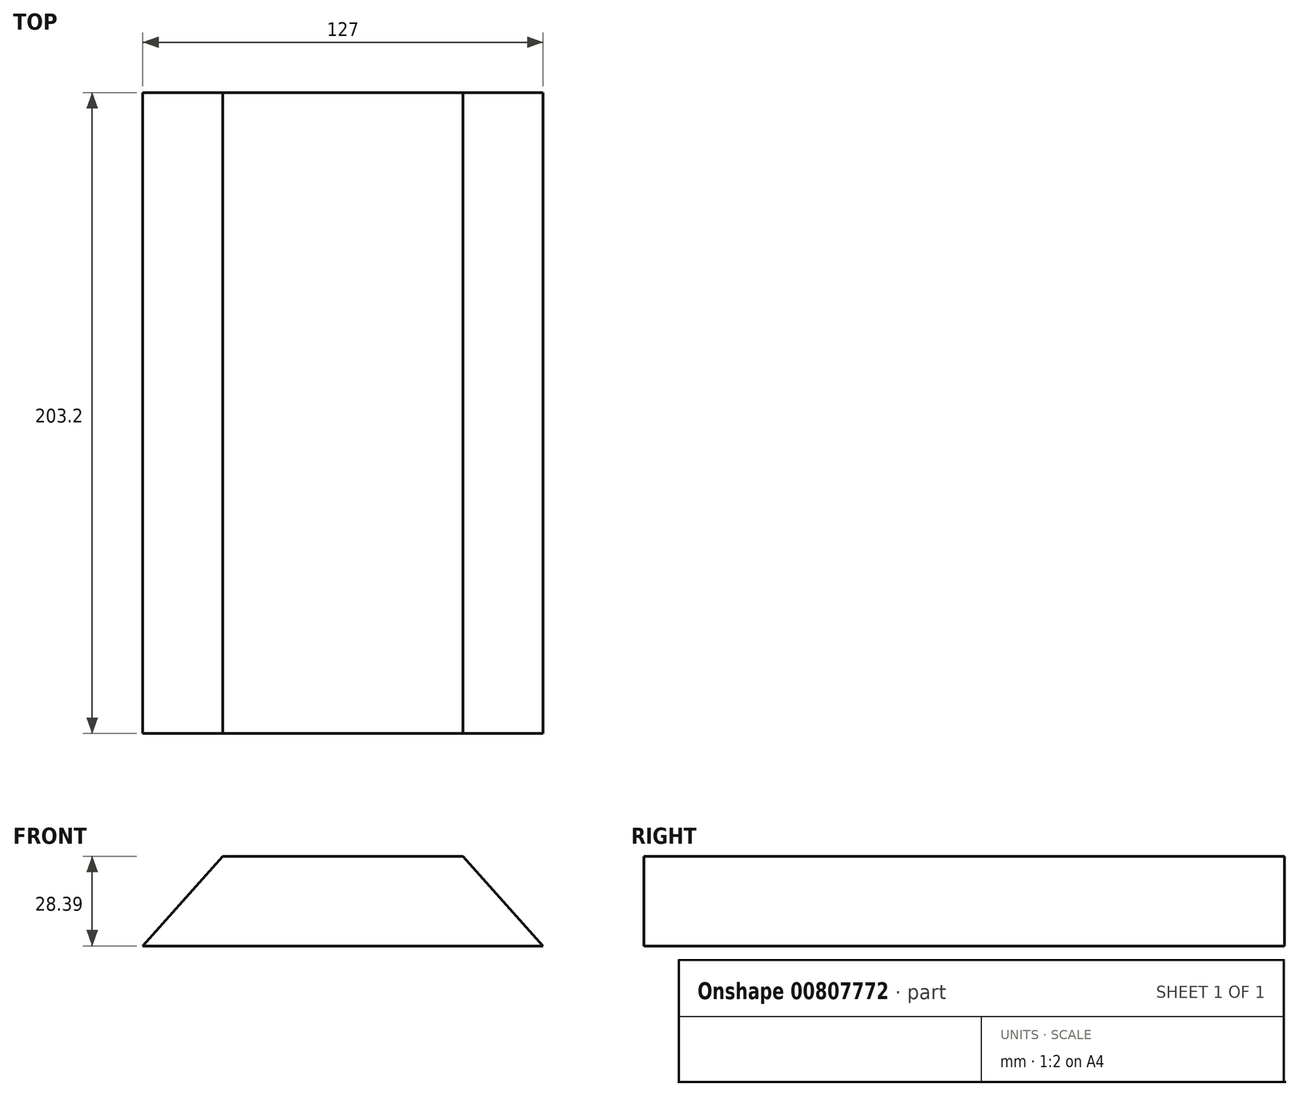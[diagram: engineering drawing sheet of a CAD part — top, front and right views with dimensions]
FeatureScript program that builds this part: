
annotation { "Feature Type Name" : "Feature", "Feature Type Description" : "" }
export const myFeature = defineFeature(function(context is Context, id is Id, definition is map)
    precondition{}
    {
        {
            var Q0;
            Q0=qCreatedBy(makeId("Front.planeOp"),FACE);
            var sketch = newSketch(context, id + "F0", { "sketchPlane" : qUnion([Q0])});
            skLineSegment(sketch, "E0", {"start": v(-79.72, -50.57) * mm, "end": v(47.28, -50.57) * mm});
            skLineSegment(sketch, "E1", {"start": v(47.28, -50.57) * mm, "end": v(21.88, -22.18) * mm});
            skLineSegment(sketch, "E2", {"start": v(21.88, -22.18) * mm, "end": v(-54.32, -22.18) * mm});
            skLineSegment(sketch, "E3", {"start": v(-79.72, -50.57) * mm, "end": v(-54.32, -22.18) * mm});
            skSolve(sketch);
        }
        {
            var Q0;
            {var subQ0=sQuery(id+"F0.wireOp",EDGE,"E1");Q0=makeQuery(id+"F0.imprint","IMPRINT",FACE,{"disambiguationData":[TD([[makeQuery(id+"F0.imprint","IMPRINT",EDGE,{"derivedFrom":subQ0}),1.0]])]});}
            extrude(context, id + "F1", {"entities" : qUnion([Q0]), "depth" : 203.2 * mm, "offsetDistance" : 25.4 * mm});
        }
    });
